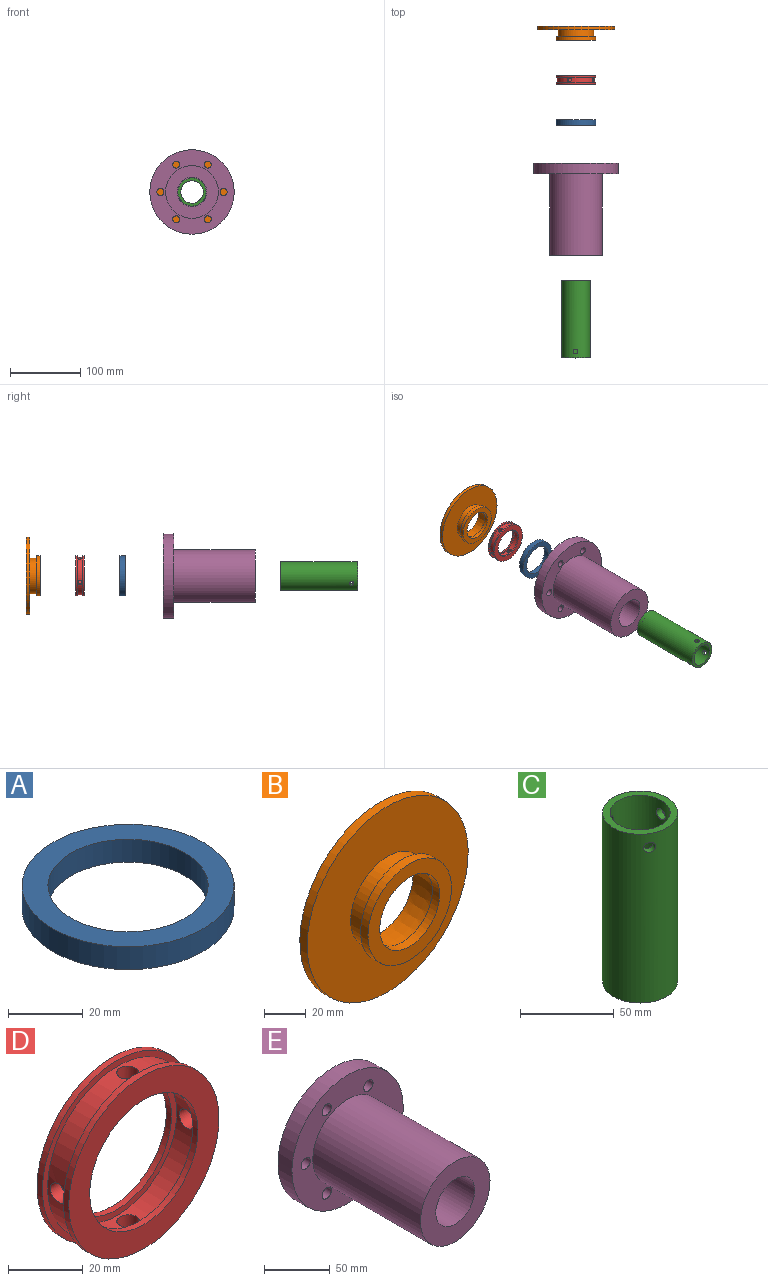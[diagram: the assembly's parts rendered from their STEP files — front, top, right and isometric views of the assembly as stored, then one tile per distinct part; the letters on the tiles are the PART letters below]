
ASSEMBLY  parts=5 mates=4
PART A: 4 faces, bbox 56.9x56.9x7.5 mm
  f0: cylinder r=21.5mm len=43mm, axis (0,0,-1), area 1013.2mm2, adj f2,f3
  f1: cylinder r=28.45mm len=56.9mm, axis (0,0,-1), area 1340.7mm2, adj f2,f3
  f2: plane 56.9x56.9mm, normal (0,0,1), area 1090.6mm2, adj f0,f1
  f3: plane 56.9x56.9mm, normal (0,0,-1), area 1090.6mm2, adj f0,f1
PART B: 10 faces, bbox 109.7x20x109.7 mm
  f0: cylinder r=20.4mm len=40.8mm, axis (0,-1,0), area 640.9mm2, adj f1,f9
  f1: plane 56.9x56.9mm, normal (0,-1,0), area 1235.4mm2, adj f0,f2
  f2: cylinder r=28.45mm len=56.9mm, axis (0,-1,0), area 893.8mm2, adj f1,f3
  f3: plane 56.9x56.9mm, normal (0,1,0), area 539.9mm2, adj f2,f4
  f4: cylinder r=25.25mm len=50.5mm, axis (0,-1,0), area 1586.5mm2, adj f3,f5
  f5: plane 109.7x109.7mm, normal (0,-1,0), area 7448.6mm2, adj f4,f6
  f6: cylinder r=54.85mm len=109.7mm, axis (0,-1,0), area 1723.2mm2, adj f5,f7
  f7: plane 109.7x109.7mm, normal (0,1,0), area 7889.3mm2, adj f6,f8
  f8: cone r=21.35mm half-angle=3.6deg, axis (0,1,0), area 2061.1mm2, adj f7,f9
  f9: plane 42.7x42.7mm, normal (0,1,0), area 124.6mm2, adj f0,f8
PART C: 11 faces, bbox 40x40x110 mm
  f0: cylinder r=3.3mm len=7.89mm, axis (0.5,0.87,0), area 83.7mm2, adj f2,f3
  f1: cylinder r=3.3mm len=7.89mm, axis (0.5,-0.87,0), area 83.7mm2, adj f2,f3
  f2: cylinder r=16mm len=100mm, axis (0,0,-1), area 9949.4mm2, adj f0,f1,f5,f9,f10
  f3: cylinder r=20mm len=110mm, axis (0,0,-1), area 13719.7mm2, adj f0,f1,f5,f6,f10
  f4: cylinder r=16mm len=32mm, axis (0,0,-1), area 502.7mm2, adj f6,f7
  f5: plane 40x40mm, normal (0,0,1), area 452.4mm2, adj f2,f3
  f6: plane 40x40mm, normal (0,0,-1), area 452.4mm2, adj f3,f4
  f7: plane 37x37mm, normal (0,0,1), area 271mm2, adj f4,f8
  f8: cylinder r=18.5mm len=37mm, axis (0,0,-1), area 581.2mm2, adj f7,f9
  f9: plane 37x37mm, normal (0,0,-1), area 271mm2, adj f2,f8
  f10: cylinder r=3.3mm len=6.6mm, axis (-1,0,0), area 83.7mm2, adj f2,f3
PART D: 16 faces, bbox 56.9x12x56.9 mm
  f0: cylinder r=26.47mm len=52.95mm, axis (0,-1,0), area 1217.6mm2, adj f5,f6,f12,f13,f14,f15
  f1: cylinder r=22.47mm len=44.95mm, axis (0,-1,0), area 1016.4mm2, adj f10,f11,f12,f13,f14,f15
  f2: cylinder r=20.5mm len=41mm, axis (0,-1,0), area 257.6mm2, adj f3,f11
  f3: plane 56.9x56.9mm, normal (0,-1,0), area 1222.6mm2, adj f2,f4
  f4: cylinder r=28.45mm len=56.9mm, axis (0,-1,0), area 357.5mm2, adj f3,f5
  f5: plane 56.9x56.9mm, normal (0,1,0), area 340.8mm2, adj f0,f4
  f6: plane 56.9x56.9mm, normal (0,-1,0), area 340.8mm2, adj f0,f7
  f7: cylinder r=28.45mm len=56.9mm, axis (0,-1,0), area 357.5mm2, adj f6,f8
  f8: plane 56.9x56.9mm, normal (0,1,0), area 1222.6mm2, adj f7,f9
  f9: cylinder r=20.5mm len=41mm, axis (0,-1,0), area 257.6mm2, adj f8,f10
  f10: plane 44.95x44.95mm, normal (0,-1,0), area 266.6mm2, adj f1,f9
  f11: plane 44.95x44.95mm, normal (0,1,0), area 266.6mm2, adj f1,f2
  f12: cylinder r=3mm len=6mm, axis (0,0,1), area 75.7mm2, adj f0,f1
  f13: cylinder r=3mm len=6mm, axis (0,0,1), area 75.7mm2, adj f0,f1
  f14: cylinder r=3mm len=6mm, axis (-1,0,0), area 75.7mm2, adj f0,f1
  f15: cylinder r=3mm len=6mm, axis (-1,0,0), area 75.7mm2, adj f0,f1
PART E: 16 faces, bbox 120x131.1x120 mm
  f0: cylinder r=5mm len=15mm, axis (0,1,0), area 471.2mm2, adj f8,f10
  f1: cylinder r=5mm len=15mm, axis (0,1,0), area 471.2mm2, adj f8,f10
  f2: cylinder r=5mm len=15mm, axis (0,1,0), area 471.2mm2, adj f8,f10
  f3: cylinder r=5mm len=15mm, axis (0,1,0), area 471.2mm2, adj f8,f10
  f4: cylinder r=5mm len=15mm, axis (0,1,0), area 471.2mm2, adj f8,f10
  f5: cylinder r=21mm len=50.5mm, axis (0,-1,0), area 6663.3mm2, adj f6,f14
  f6: plane 75x75mm, normal (0,-1,0), area 3032.4mm2, adj f5,f7
  f7: cylinder r=37.5mm len=116.1mm, axis (0,-1,0), area 27355.4mm2, adj f6,f8
  f8: plane 120x120mm, normal (0,-1,0), area 6420.6mm2, adj f0,f1,f2,f3,f4,f7,f9,f15
  f9: cylinder r=60mm len=120mm, axis (0,-1,0), area 5654.9mm2, adj f8,f10
  f10: plane 120x120mm, normal (0,1,0), area 8304.6mm2, adj f0,f1,f2,f3,f4,f9,f11,f15
  f11: cylinder r=28.4mm len=70.6mm, axis (0,-1,0), area 12598mm2, adj f10,f12
  f12: plane 56.8x56.8mm, normal (0,1,0), area 1588.2mm2, adj f11,f13
  f13: cylinder r=17.35mm len=34.7mm, axis (0,-1,0), area 1090.1mm2, adj f12,f14
  f14: plane 42x42mm, normal (0,-1,0), area 439.8mm2, adj f5,f13
  f15: cylinder r=5mm len=15mm, axis (0,1,0), area 471.2mm2, adj f8,f10
PLACE A rot(axis=(-0.86,0.36,0.36),98.6deg) t=(0.23,119.69,0.04)mm
PLACE B rot(axis=(0,1,0),51.5deg) t=(0.23,240.82,0.04)mm
PLACE C rot(axis=(0.56,-0.58,0.58),121.3deg) t=(0.23,-156.39,0.04)mm
PLACE D rot(axis=(0,-1,0),21.1deg) t=(0.23,178.21,0.04)mm
PLACE E t=(0.23,-65.39,0.04)mm fixed
MATE cylindrical D.f0 <-> E.f5  axis (0,-1,0) through (0.23,184.21,0.04)mm
MATE cylindrical A.f1 <-> E.f5  axis (0,-1,0) through (0.23,123.44,0.04)mm
MATE cylindrical C.f3 <-> E.f5  axis (0,1,0) through (0.23,-156.39,0.04)mm
MATE cylindrical B.f0 <-> E.f5  axis (0,1,0) through (0.23,253.32,0.04)mm
